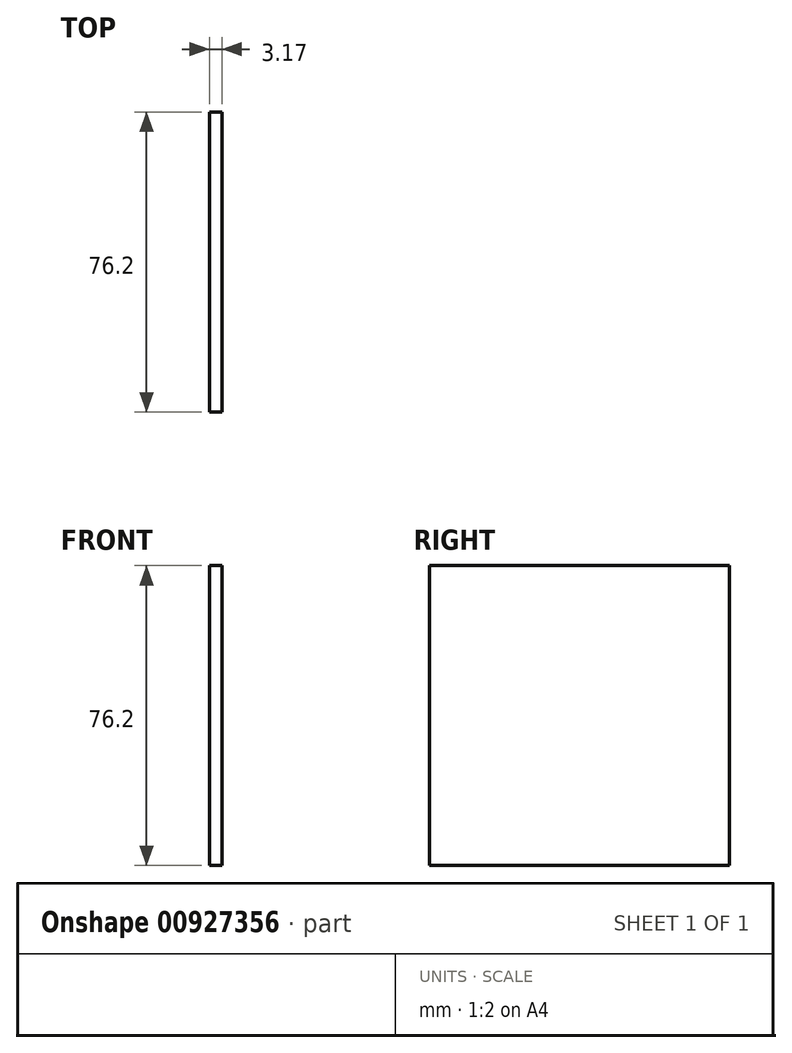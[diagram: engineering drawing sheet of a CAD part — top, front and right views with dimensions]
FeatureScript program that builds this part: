
annotation { "Feature Type Name" : "Feature", "Feature Type Description" : "" }
export const myFeature = defineFeature(function(context is Context, id is Id, definition is map)
    precondition{}
    {
        {
            var Q0;
            Q0=qCreatedBy(makeId("Right.planeOp"),FACE);
            var sketch = newSketch(context, id + "F0", { "sketchPlane" : qUnion([Q0])});
            skLineSegment(sketch, "E0.bottom", {"start": v(-38.1, 38.1) * mm, "end": v(38.1, 38.1) * mm});
            skLineSegment(sketch, "E0.top", {"start": v(-38.1, -38.1) * mm, "end": v(38.1, -38.1) * mm});
            skLineSegment(sketch, "E0.left", {"start": v(-38.1, 38.1) * mm, "end": v(-38.1, -38.1) * mm});
            skLineSegment(sketch, "E0.right", {"start": v(38.1, 38.1) * mm, "end": v(38.1, -38.1) * mm});
            skSolve(sketch);
        }
        {
            var Q0;
            Q0=makeQuery(id+"F0.imprint","IMPRINT",FACE,{"disambiguationData":[TD([[makeQuery(id+"F0.imprint","IMPRINT",EDGE,{"derivedFrom":sQuery(id+"F0.wireOp",EDGE,"E0.bottom")}),-1.0]])]});
            extrude(context, id + "F1", {"entities" : qUnion([Q0]), "depth" : 3.17 * mm, "offsetDistance" : 25.4 * mm});
        }
    });
